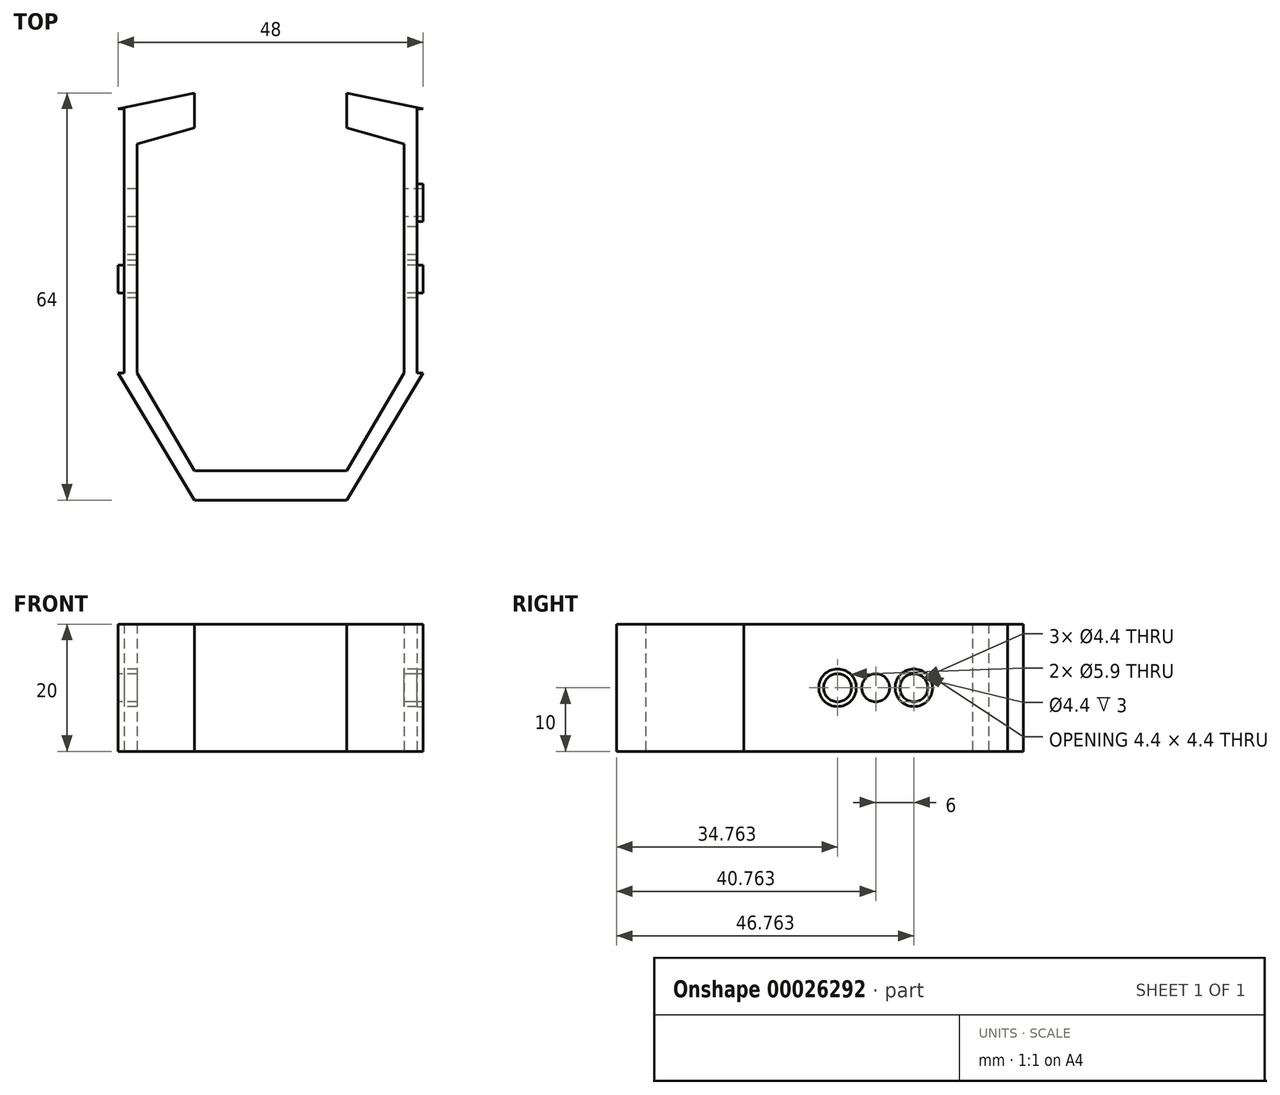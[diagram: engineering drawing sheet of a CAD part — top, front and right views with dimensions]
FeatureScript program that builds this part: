
annotation { "Feature Type Name" : "Feature", "Feature Type Description" : "" }
export const myFeature = defineFeature(function(context is Context, id is Id, definition is map)
    precondition{}
    {
        {
            var Q0;
            Q0=qCreatedBy(makeId("Top.planeOp"),FACE);
            var sketch = newSketch(context, id + "F0", { "sketchPlane" : qUnion([Q0])});
            skPoint(sketch, "E0", {"position": v(-12, 0) * mm});
            skLineSegment(sketch, "E1", {"start": v(-12, 0) * mm, "end": v(12, 0) * mm, "construction": true});
            skLineSegment(sketch, "E2", {"start": v(-12, 0) * mm, "end": v(-12, 36) * mm, "construction": true});
            skLineSegment(sketch, "E3", {"start": v(-12, 36) * mm, "end": v(12, 36) * mm, "construction": true});
            skLineSegment(sketch, "E4", {"start": v(-12, 0) * mm, "end": v(-12, -35.4) * mm, "construction": true});
            skPoint(sketch, "E5", {"position": v(-12, -20) * mm});
            skLineSegment(sketch, "E6", {"start": v(-12, 36) * mm, "end": v(-12, 51.76) * mm, "construction": true});
            skPoint(sketch, "E7", {"position": v(-12, 44) * mm});
            skLineSegment(sketch, "E8", {"start": v(-12, 38.5) * mm, "end": v(-12, 44) * mm});
            skLineSegment(sketch, "E9", {"start": v(12, 36) * mm, "end": v(12, 0) * mm, "construction": true});
            skLineSegment(sketch, "E10", {"start": v(-12, 36) * mm, "end": v(-21, 36) * mm, "construction": true});
            skLineSegment(sketch, "E11", {"start": v(-21, 36) * mm, "end": v(-21, 0) * mm});
            skLineSegment(sketch, "E12", {"start": v(-21, 36) * mm, "end": v(-12, 38.5) * mm});
            skLineSegment(sketch, "E13", {"start": v(-24, 0) * mm, "end": v(-12, -20) * mm});
            skLineSegment(sketch, "E14", {"start": v(-21, 0) * mm, "end": v(-12, -15.41) * mm});
            skLineSegment(sketch, "E15", {"start": v(-12, 44) * mm, "end": v(-24, 41.53) * mm});
            skLineSegment(sketch, "E16", {"start": v(-24, 0) * mm, "end": v(-24, 41.53) * mm});
            skLineSegment(sketch, "E17.MirrorCS", {"start": v(24, 0) * mm, "end": v(24, 41.53) * mm});
            skLineSegment(sketch, "E18.MirrorCS", {"start": v(21, 36) * mm, "end": v(21, 0) * mm});
            skLineSegment(sketch, "E19.MirrorCS", {"start": v(21, 36) * mm, "end": v(12, 38.5) * mm});
            skLineSegment(sketch, "E20.MirrorCS", {"start": v(12, 44) * mm, "end": v(24, 41.53) * mm});
            skLineSegment(sketch, "E21.MirrorCS", {"start": v(24, 0) * mm, "end": v(12, -20) * mm});
            skLineSegment(sketch, "E22.MirrorCS", {"start": v(21, 0) * mm, "end": v(12, -15.41) * mm});
            skLineSegment(sketch, "E23", {"start": v(12, 44) * mm, "end": v(12, 38.5) * mm});
            skLineSegment(sketch, "E24", {"start": v(-12, -15.41) * mm, "end": v(12, -15.41) * mm});
            skLineSegment(sketch, "E25", {"start": v(12, -20) * mm, "end": v(-12, -20) * mm});
            skSolve(sketch);
        }
        {
            var Q0;
            Q0=makeQuery(id+"F0.imprint","IMPRINT",FACE,{"disambiguationData":[TD([[makeQuery(id+"F0.imprint","IMPRINT",EDGE,{"derivedFrom":sQuery(id+"F0.wireOp",EDGE,"E11")}),-1.0]])]});
            extrude(context, id + "F1", {"entities" : qUnion([Q0]), "depth" : 20 * mm});
        }
        {
            var Q0;
            Q0=makeQuery(id+"F1.opExtrude","SWEPT_FACE",FACE,{"disambiguationData":[OSD([sQuery(id+"F0.wireOp",EDGE,"E17.MirrorCS")])]});
            var sketch = newSketch(context, id + "F2", { "sketchPlane" : qUnion([Q0])});
            skLineSegment(sketch, "E26", {"start": v(0, 10) * mm, "end": v(41.53, 10) * mm, "construction": true});
            skLineSegment(sketch, "E27", {"start": v(20.76, 20) * mm, "end": v(20.76, 0) * mm, "construction": true});
            skCircle(sketch, "E28", {"center": v(20.76, 10) * mm, "radius": 2.95 * mm});
            skCircle(sketch, "E29", {"center": v(20.76, 10) * mm, "radius": 2.2 * mm});
            skCircle(sketch, "E30", {"center": v(14.76, 10) * mm, "radius": 2.95 * mm});
            skCircle(sketch, "E31", {"center": v(14.76, 10) * mm, "radius": 2.2 * mm});
            skCircle(sketch, "E32.MirrorC", {"center": v(26.76, 10) * mm, "radius": 2.95 * mm});
            skCircle(sketch, "E33.MirrorC", {"center": v(26.76, 10) * mm, "radius": 2.2 * mm});
            skSolve(sketch);
        }
        {
            var Q0;
            Q0=makeQuery(id+"F1.opExtrude","SWEPT_FACE",FACE,{"disambiguationData":[OSD([sQuery(id+"F0.wireOp",EDGE,"E16")])]});
            var sketch = newSketch(context, id + "F3", { "sketchPlane" : qUnion([Q0])});
            skLineSegment(sketch, "E34", {"start": v(-41.53, 10) * mm, "end": v(0, 10) * mm, "construction": true});
            skLineSegment(sketch, "E35", {"start": v(-20.76, 20) * mm, "end": v(-20.76, 0) * mm, "construction": true});
            skCircle(sketch, "E36", {"center": v(-20.76, 10) * mm, "radius": 2.95 * mm});
            skCircle(sketch, "E37", {"center": v(-20.76, 10) * mm, "radius": 2.2 * mm});
            skCircle(sketch, "E38", {"center": v(-26.76, 10) * mm, "radius": 2.95 * mm});
            skCircle(sketch, "E39", {"center": v(-26.76, 10) * mm, "radius": 2.2 * mm});
            skCircle(sketch, "E40.MirrorC", {"center": v(-14.76, 10) * mm, "radius": 2.95 * mm});
            skCircle(sketch, "E41.MirrorC", {"center": v(-14.76, 10) * mm, "radius": 2.2 * mm});
            skSolve(sketch);
        }
        {
            var Q0;
            Q0=makeQuery(id+"F3.imprint","IMPRINT",FACE,{"disambiguationData":[TD([[makeQuery(id+"F3.imprint","IMPRINT",EDGE,{"derivedFrom":sQuery(id+"F3.wireOp",EDGE,"E39")}),1.0]])]});
            var Q1;
            Q1=makeQuery(id+"F3.imprint","IMPRINT",FACE,{"disambiguationData":[TD([[makeQuery(id+"F3.imprint","IMPRINT",EDGE,{"derivedFrom":sQuery(id+"F3.wireOp",EDGE,"E37")}),1.0]])]});
            var Q2;
            Q2=makeQuery(id+"F3.imprint","IMPRINT",FACE,{"disambiguationData":[TD([[makeQuery(id+"F3.imprint","IMPRINT",EDGE,{"derivedFrom":sQuery(id+"F3.wireOp",EDGE,"E41.MirrorC")}),-1.0]])]});
            extrude(context, id + "F4", {"entities" : qUnion([Q0, Q1, Q2]), "operationType" : NewBodyOperationType.REMOVE, "endBound" : BoundingType.THROUGH_ALL, "oppositeDirection" : true, "depth" : 25 * mm});
        }
        {
            var Q0;
            Q0=makeQuery(id+"F2.imprint","IMPRINT",FACE,{"disambiguationData":[TD([[makeQuery(id+"F2.imprint","IMPRINT",EDGE,{"derivedFrom":sQuery(id+"F2.wireOp",EDGE,"E30")}),1.0]])]});
            var Q1;
            Q1=makeQuery(id+"F2.imprint","IMPRINT",FACE,{"disambiguationData":[TD([[makeQuery(id+"F2.imprint","IMPRINT",EDGE,{"derivedFrom":sQuery(id+"F2.wireOp",EDGE,"E28")}),1.0]])]});
            var Q2;
            Q2=makeQuery(id+"F2.imprint","IMPRINT",FACE,{"disambiguationData":[TD([[makeQuery(id+"F2.imprint","IMPRINT",EDGE,{"derivedFrom":sQuery(id+"F2.wireOp",EDGE,"E32.MirrorC")}),-1.0]])]});
            extrude(context, id + "F5", {"entities" : qUnion([Q0, Q1, Q2]), "operationType" : NewBodyOperationType.REMOVE, "oppositeDirection" : true, "depth" : 1 * mm});
        }
        {
            var Q0;
            Q0=makeQuery(id+"F3.imprint","IMPRINT",FACE,{"disambiguationData":[TD([[makeQuery(id+"F3.imprint","IMPRINT",EDGE,{"derivedFrom":sQuery(id+"F3.wireOp",EDGE,"E40.MirrorC")}),-1.0]])]});
            var Q1;
            Q1=makeQuery(id+"F3.imprint","IMPRINT",FACE,{"disambiguationData":[TD([[makeQuery(id+"F3.imprint","IMPRINT",EDGE,{"derivedFrom":sQuery(id+"F3.wireOp",EDGE,"E36")}),1.0]])]});
            var Q2;
            Q2=makeQuery(id+"F3.imprint","IMPRINT",FACE,{"disambiguationData":[TD([[makeQuery(id+"F3.imprint","IMPRINT",EDGE,{"derivedFrom":sQuery(id+"F3.wireOp",EDGE,"E38")}),1.0]])]});
            extrude(context, id + "F6", {"entities" : qUnion([Q0, Q1, Q2]), "operationType" : NewBodyOperationType.REMOVE, "oppositeDirection" : true, "depth" : 1 * mm});
        }
    });
